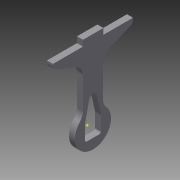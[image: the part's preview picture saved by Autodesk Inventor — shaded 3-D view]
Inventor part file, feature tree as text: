
AUTODESK INVENTOR PART (.ipt)
format: ipt  version: 2015 (Build 190159000, 159)  size: 132,608 bytes
history: native  units: mm
features: extrude x1, sketch x1
ambient origin geometry x8: Origin, YZ Plane, XZ Plane, XY Plane, X Axis, Y Axis, Z Axis, Center Point
bodies: Body1 (feature_tree)
feature tree (2):
  extrude  "Extrusion6"  Depth=3.0mm
  sketch  "Sketch1"  dims[d8=22.5deg d16=3.0mm d25=10.0mm d32=6.0mm d33=6.0mm d68=18.0mm d69=6.0mm d70=38.0mm d74=22.5deg d75=8.0mm d76=8.0mm d77=4.0mm d78=13.0mm d79=6.0mm d80=1.0mm d81=90.0mm d82=46.0mm d84=38.0mm d85=3.0mm d86=5.0mm d87=20.0mm d88=40.0mm d90=2.0mm d93=1.0mm d94=1.0mm d95=22.5deg d96=22.5deg d97=4.0mm d98=4.0mm d101=3.0mm d102=0.0mm]
